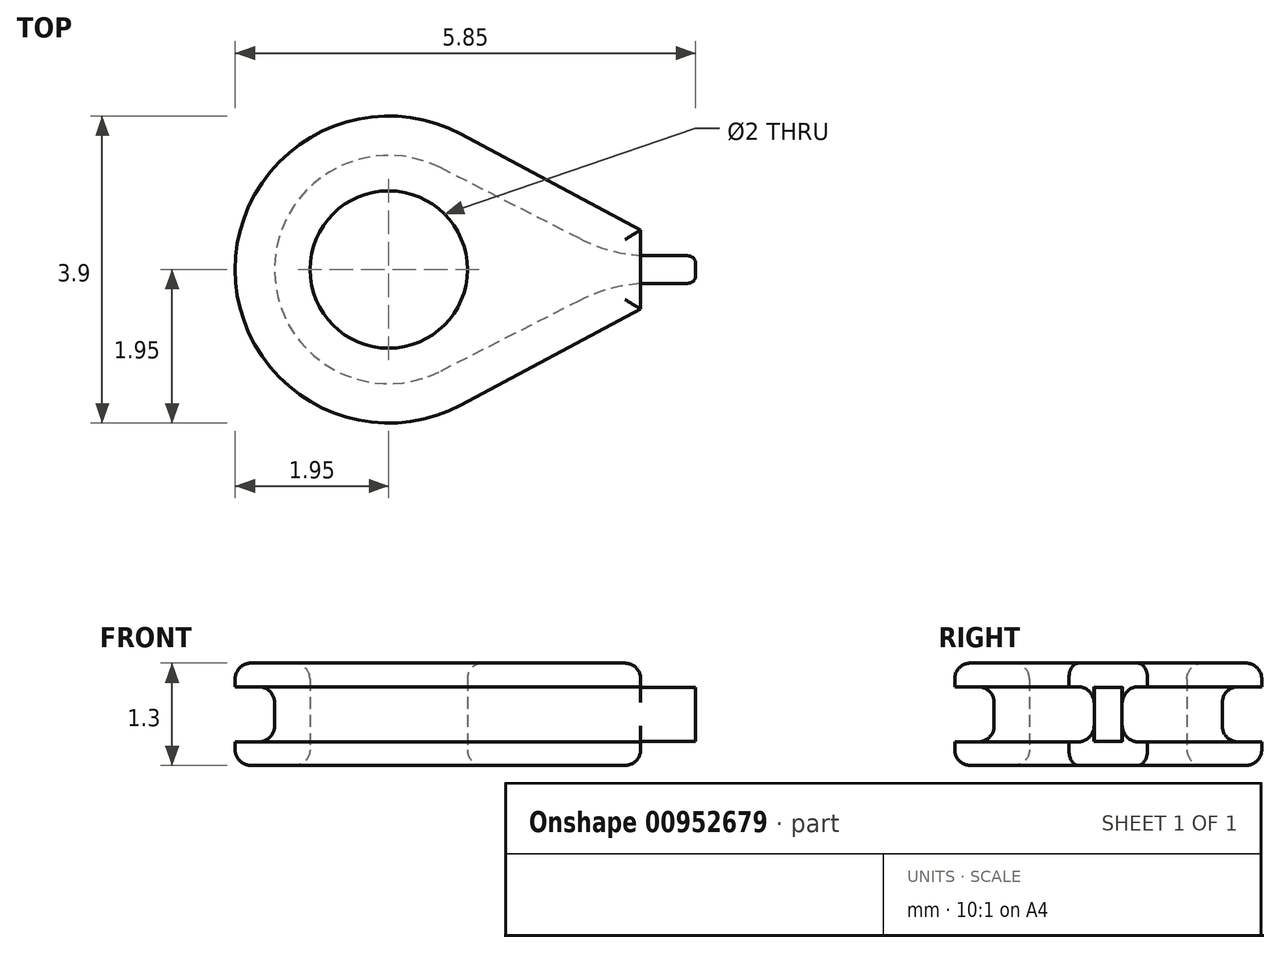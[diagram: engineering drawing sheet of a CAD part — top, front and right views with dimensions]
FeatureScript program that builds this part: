
annotation { "Feature Type Name" : "Feature", "Feature Type Description" : "" }
export const myFeature = defineFeature(function(context is Context, id is Id, definition is map)
    precondition{}
    {
        {
            var Q0;
            Q0=qCreatedBy(makeId("Top.planeOp"),FACE);
            var sketch = newSketch(context, id + "F0", { "sketchPlane" : qUnion([Q0])});
            skCircle(sketch, "E0", {"center": v(0, 0) * mm, "radius": 1 * mm});
            skLineSegment(sketch, "E1", {"start": v(3.2, -0.17) * mm, "end": v(3.2, -0.5) * mm});
            skPoint(sketch, "E2.0.end.orphan", {"position": v(3.2, 0) * mm});
            skPoint(sketch, "E3.MirrorCS.start.orphan", {"position": v(3.2, 0.5) * mm});
            skArc(sketch, "E4", {"start": v(0.92, 1.72) * mm, "mid": v(-1.95, 0) * mm, "end": v(0.92, -1.72) * mm});
            skArc(sketch, "E5", {"start": v(0.66, 1.3) * mm, "mid": v(-1.45, 0) * mm, "end": v(0.66, -1.3) * mm});
            skLineSegment(sketch, "E6", {"start": v(3.2, 0.5) * mm, "end": v(0.92, 1.72) * mm});
            skLineSegment(sketch, "E7", {"start": v(3.2, -0.5) * mm, "end": v(0.92, -1.72) * mm});
            skLineSegment(sketch, "E8", {"start": v(2.43, 0.4) * mm, "end": v(0.66, 1.3) * mm});
            skLineSegment(sketch, "E9", {"start": v(2.43, -0.4) * mm, "end": v(0.66, -1.3) * mm});
            skLineSegment(sketch, "E10", {"start": v(3.33, 0.17) * mm, "end": v(3.8, 0.17) * mm});
            skLineSegment(sketch, "E11", {"start": v(3.9, 0.08) * mm, "end": v(3.9, 0) * mm});
            skLineSegment(sketch, "E12.MirrorCS", {"start": v(3.33, -0.17) * mm, "end": v(3.8, -0.17) * mm});
            skLineSegment(sketch, "E13.MirrorCS", {"start": v(3.9, -0.07) * mm, "end": v(3.9, 0) * mm});
            skLineSegment(sketch, "E14", {"start": v(3.2, 0.5) * mm, "end": v(3.2, 0.17) * mm});
            skPoint(sketch, "E15.visualSharp", {"position": v(2.86, 0.18) * mm});
            skArc(sketch, "E15.filletArc", {"start": v(2.43, 0.4) * mm, "mid": v(2.87, 0.23) * mm, "end": v(3.33, 0.17) * mm});
            skPoint(sketch, "E16.visualSharp", {"position": v(2.86, -0.18) * mm});
            skArc(sketch, "E16.filletArc", {"start": v(3.33, -0.17) * mm, "mid": v(2.87, -0.23) * mm, "end": v(2.43, -0.4) * mm});
            skPoint(sketch, "E17.visualSharp", {"position": v(3.9, 0.17) * mm});
            skArc(sketch, "E17.filletArc", {"start": v(3.9, 0.08) * mm, "mid": v(3.87, 0.15) * mm, "end": v(3.8, 0.17) * mm});
            skPoint(sketch, "E18.visualSharp", {"position": v(3.9, -0.17) * mm});
            skArc(sketch, "E18.filletArc", {"start": v(3.8, -0.17) * mm, "mid": v(3.87, -0.15) * mm, "end": v(3.9, -0.07) * mm});
            skLineSegment(sketch, "E19", {"start": v(3.2, 0.17) * mm, "end": v(3.2, -0.17) * mm, "construction": true});
            skSolve(sketch);
        }
        {
            var Q0;
            Q0=makeQuery(id+"F0.imprint","IMPRINT",FACE,{"disambiguationData":[TD([[makeQuery(id+"F0.imprint","IMPRINT",EDGE,{"derivedFrom":sQuery(id+"F0.wireOp",EDGE,"E0")}),-1.0]])]});
            extrude(context, id + "F1", {"entities" : qUnion([Q0]), "depth" : 1.3 * mm, "offsetDistance" : 25 * mm});
        }
        {
            var Q0;
            Q0=makeQuery(id+"F0.imprint","IMPRINT",FACE,{"disambiguationData":[TD([[makeQuery(id+"F0.imprint","IMPRINT",EDGE,{"derivedFrom":sQuery(id+"F0.wireOp",EDGE,"E1")}),-1.0]])]});
            var Q1;
            Q1=makeQuery(id+"F0.imprint","IMPRINT",FACE,{"disambiguationData":[TD([[makeQuery(id+"F0.imprint","IMPRINT",EDGE,{"derivedFrom":sQuery(id+"F0.wireOp",EDGE,"E0")}),-1.0]])]});
            extrude(context, id + "F2", {"entities" : qUnion([Q0, Q1]), "operationType" : NewBodyOperationType.ADD, "depth" : 0.3 * mm, "offsetDistance" : 25 * mm});
        }
        {
            var Q0;
            Q0 = qSketchRegion(id + "F0", true);
            extrude(context, id + "F3", {"entities" : qUnion([Q0]), "operationType" : NewBodyOperationType.ADD, "depth" : 1.3 * mm, "offsetDistance" : 25 * mm, "hasSecondDirection" : true, "secondDirectionOppositeDirection" : false, "secondDirectionDepth" : 1 * mm});
        }
        {
            var Q0;
            Q0=makeQuery(id+"F1.opExtrude","SWEPT_FACE",FACE,{"disambiguationData":[OSD([sQuery(id+"F0.wireOp",EDGE,"E11"),sQuery(id+"F0.wireOp",EDGE,"E13.MirrorCS")])]});
            var sketch = newSketch(context, id + "F4", { "sketchPlane" : qUnion([Q0])});
            skLineSegment(sketch, "E20", {"start": v(-0.3, 1.3) * mm, "end": v(0.29, 1.3) * mm});
            skLineSegment(sketch, "E21", {"start": v(0.29, 1.3) * mm, "end": v(0.29, 1) * mm});
            skLineSegment(sketch, "E22", {"start": v(0.29, 1) * mm, "end": v(-0.3, 1) * mm});
            skLineSegment(sketch, "E23", {"start": v(-0.3, 1) * mm, "end": v(-0.3, 1.3) * mm});
            skLineSegment(sketch, "E24", {"start": v(-0.3, 0.3) * mm, "end": v(0.3, 0.3) * mm});
            skLineSegment(sketch, "E25", {"start": v(0.3, 0.3) * mm, "end": v(0.3, 0) * mm});
            skLineSegment(sketch, "E26", {"start": v(0.3, 0) * mm, "end": v(-0.3, 0) * mm});
            skLineSegment(sketch, "E27", {"start": v(-0.3, 0) * mm, "end": v(-0.3, 0.3) * mm});
            skSolve(sketch);
        }
        {
            var Q0;
            {var subQ3=sQuery(id+"F4.wireOp",EDGE,"E23");Q0=makeQuery(id+"F4.imprint","IMPRINT",FACE,{"disambiguationData":[TD([[makeQuery(id+"F4.imprint","IMPRINT",EDGE,{"derivedFrom":subQ3}),-1.0]])]});}
            var Q1;
            {var subQ0=sQuery(id+"F4.wireOp",EDGE,"E20");var subQ1=makeQuery(id+"F1.opExtrude","SWEPT_EDGE",EDGE,{"disambiguationData":[OSD([sQuery(id+"F0.wireOp",EDGE,"E11"),sQuery(id+"F0.wireOp",EDGE,"E17.filletArc")])]});var subQ2=makeQuery(id+"F4.imprint","INTERSECT",VERTEX,{"derivedFrom":[subQ1,subQ0]});Q1=makeQuery(id+"F4.imprint","IMPRINT",FACE,{"disambiguationData":[TD([[makeQuery(id+"F4.imprint","IMPRINT",EDGE,{"disambiguationData":[TD([[subQ2,1.0]])],"derivedFrom":subQ0}),-1.0]])]});}
            var Q2;
            {var subQ3=sQuery(id+"F4.wireOp",EDGE,"E21");Q2=makeQuery(id+"F4.imprint","IMPRINT",FACE,{"disambiguationData":[TD([[makeQuery(id+"F4.imprint","IMPRINT",EDGE,{"derivedFrom":subQ3}),-1.0]])]});}
            var Q3;
            {var subQ0=sQuery(id+"F4.wireOp",EDGE,"E25");Q3=makeQuery(id+"F4.imprint","IMPRINT",FACE,{"disambiguationData":[TD([[makeQuery(id+"F4.imprint","IMPRINT",EDGE,{"derivedFrom":subQ0}),-1.0]])]});}
            var Q4;
            {var subQ0=sQuery(id+"F4.wireOp",EDGE,"E24");var subQ1=makeQuery(id+"F1.opExtrude","SWEPT_EDGE",EDGE,{"disambiguationData":[OSD([sQuery(id+"F0.wireOp",EDGE,"E13.MirrorCS"),sQuery(id+"F0.wireOp",EDGE,"E18.filletArc")])]});var subQ2=makeQuery(id+"F4.imprint","INTERSECT",VERTEX,{"derivedFrom":[subQ1,subQ0]});Q4=makeQuery(id+"F4.imprint","IMPRINT",FACE,{"disambiguationData":[TD([[makeQuery(id+"F4.imprint","IMPRINT",EDGE,{"disambiguationData":[TD([[subQ2,-1.0]])],"derivedFrom":subQ0}),-1.0]])]});}
            var Q5;
            {var subQ0=sQuery(id+"F4.wireOp",EDGE,"E27");Q5=makeQuery(id+"F4.imprint","IMPRINT",FACE,{"disambiguationData":[TD([[makeQuery(id+"F4.imprint","IMPRINT",EDGE,{"derivedFrom":subQ0}),-1.0]])]});}
            extrude(context, id + "F5", {"entities" : qUnion([Q0, Q1, Q2, Q3, Q4, Q5]), "operationType" : NewBodyOperationType.REMOVE, "oppositeDirection" : true, "depth" : 0.7 * mm, "offsetDistance" : 25 * mm});
        }
        {
            var Q0;
            {var subQ0=sQuery(id+"F0.wireOp",EDGE,"E18.filletArc");var subQ1=sQuery(id+"F0.wireOp",EDGE,"E17.filletArc");var subQ2=sQuery(id+"F0.wireOp",EDGE,"E16.filletArc");var subQ3=sQuery(id+"F0.wireOp",EDGE,"E15.filletArc");var subQ4=sQuery(id+"F0.wireOp",EDGE,"E13.MirrorCS");var subQ5=sQuery(id+"F0.wireOp",EDGE,"E12.MirrorCS");var subQ6=sQuery(id+"F0.wireOp",EDGE,"E11");var subQ7=sQuery(id+"F0.wireOp",EDGE,"E10");var subQ8=sQuery(id+"F0.wireOp",EDGE,"E0");Q0=makeQuery(id+"F3.boolean.opBoolean","MERGE",FACE,{"derivedFrom":[makeQuery(id+"F1.opExtrude","CAP_FACE",FACE,{"disambiguationData":[OSD([subQ8,sQuery(id+"F0.wireOp",EDGE,"E5"),sQuery(id+"F0.wireOp",EDGE,"E8"),sQuery(id+"F0.wireOp",EDGE,"E9"),subQ7,subQ6,subQ5,subQ4,subQ3,subQ2,subQ1,subQ0])],"isStart":false}),makeQuery(id+"F3.opExtrude","CAP_FACE",FACE,{"disambiguationData":[OSD([subQ8,sQuery(id+"F0.wireOp",EDGE,"E1"),sQuery(id+"F0.wireOp",EDGE,"E4"),sQuery(id+"F0.wireOp",EDGE,"E6"),sQuery(id+"F0.wireOp",EDGE,"E7"),subQ7,subQ6,subQ5,subQ4,sQuery(id+"F0.wireOp",EDGE,"E14"),subQ3,subQ2,subQ1,subQ0])],"isStart":false})]});}
            var Q1;
            {var subQ0=sQuery(id+"F0.wireOp",EDGE,"E18.filletArc");var subQ1=sQuery(id+"F0.wireOp",EDGE,"E17.filletArc");var subQ2=sQuery(id+"F0.wireOp",EDGE,"E16.filletArc");var subQ3=sQuery(id+"F0.wireOp",EDGE,"E15.filletArc");var subQ4=sQuery(id+"F0.wireOp",EDGE,"E13.MirrorCS");var subQ5=sQuery(id+"F0.wireOp",EDGE,"E12.MirrorCS");var subQ6=sQuery(id+"F0.wireOp",EDGE,"E11");var subQ7=sQuery(id+"F0.wireOp",EDGE,"E10");var subQ8=sQuery(id+"F0.wireOp",EDGE,"E0");Q1=makeQuery(id+"F2.boolean.opBoolean","MERGE",FACE,{"derivedFrom":[makeQuery(id+"F1.opExtrude","CAP_FACE",FACE,{"disambiguationData":[OSD([subQ8,sQuery(id+"F0.wireOp",EDGE,"E5"),sQuery(id+"F0.wireOp",EDGE,"E8"),sQuery(id+"F0.wireOp",EDGE,"E9"),subQ7,subQ6,subQ5,subQ4,subQ3,subQ2,subQ1,subQ0])],"isStart":true}),makeQuery(id+"F2.opExtrude","CAP_FACE",FACE,{"disambiguationData":[OSD([subQ8,sQuery(id+"F0.wireOp",EDGE,"E1"),sQuery(id+"F0.wireOp",EDGE,"E4"),sQuery(id+"F0.wireOp",EDGE,"E6"),sQuery(id+"F0.wireOp",EDGE,"E7"),subQ7,subQ6,subQ5,subQ4,sQuery(id+"F0.wireOp",EDGE,"E14"),subQ3,subQ2,subQ1,subQ0])],"isStart":true})]});}
            var Q2;
            Q2=makeQuery(id+"F1.opExtrude","SWEPT_FACE",FACE,{"disambiguationData":[OSD([sQuery(id+"F0.wireOp",EDGE,"E9")])]});
            fillet(context, id + "F6", {"entities" : qUnion([Q0, Q1, Q2]), "radius" : 0.2 * mm, "tangentPropagation" : true, "allowEdgeOverflow" : false});
        }
    });
